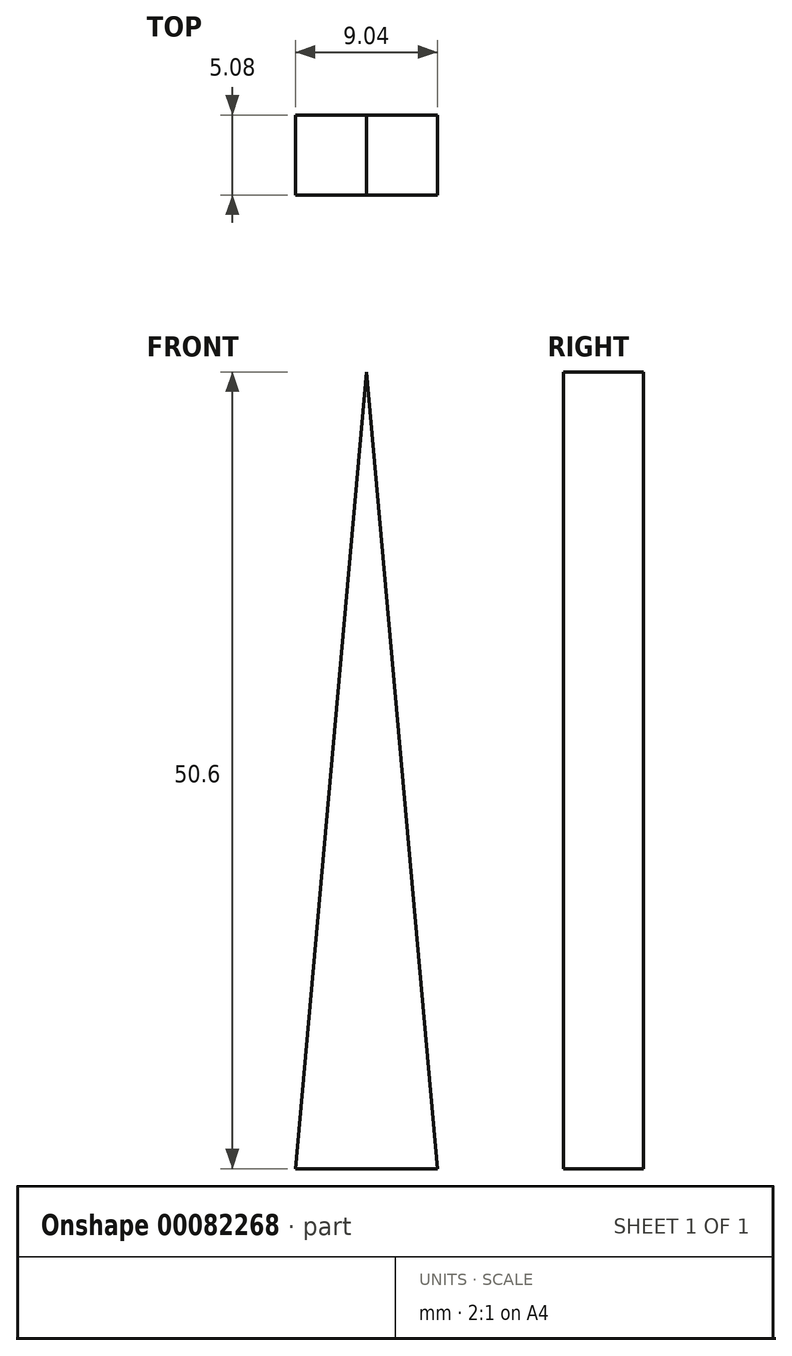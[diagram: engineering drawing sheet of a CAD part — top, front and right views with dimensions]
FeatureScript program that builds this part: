
annotation { "Feature Type Name" : "Feature", "Feature Type Description" : "" }
export const myFeature = defineFeature(function(context is Context, id is Id, definition is map)
    precondition{}
    {
        {
            var Q0;
            Q0=qCreatedBy(makeId("Front.planeOp"),FACE);
            var sketch = newSketch(context, id + "F0", { "sketchPlane" : qUnion([Q0])});
            skLineSegment(sketch, "E0", {"start": v(0, -46.98) * mm, "end": v(0, 77.1) * mm, "construction": true});
            skLineSegment(sketch, "E1", {"start": v(0, 77.1) * mm, "end": v(-4.52, 26.5) * mm});
            skLineSegment(sketch, "E2.MirrorCS", {"start": v(0, 77.1) * mm, "end": v(4.52, 26.5) * mm});
            skLineSegment(sketch, "E3", {"start": v(-4.52, 26.5) * mm, "end": v(4.52, 26.5) * mm});
            skSolve(sketch);
        }
        {
            var Q0;
            Q0 = qSketchRegion(id + "F0", true);
            extrude(context, id + "F1", {"entities" : qUnion([Q0]), "endBound" : BoundingType.SYMMETRIC, "depth" : 5.08 * mm});
        }
    });
